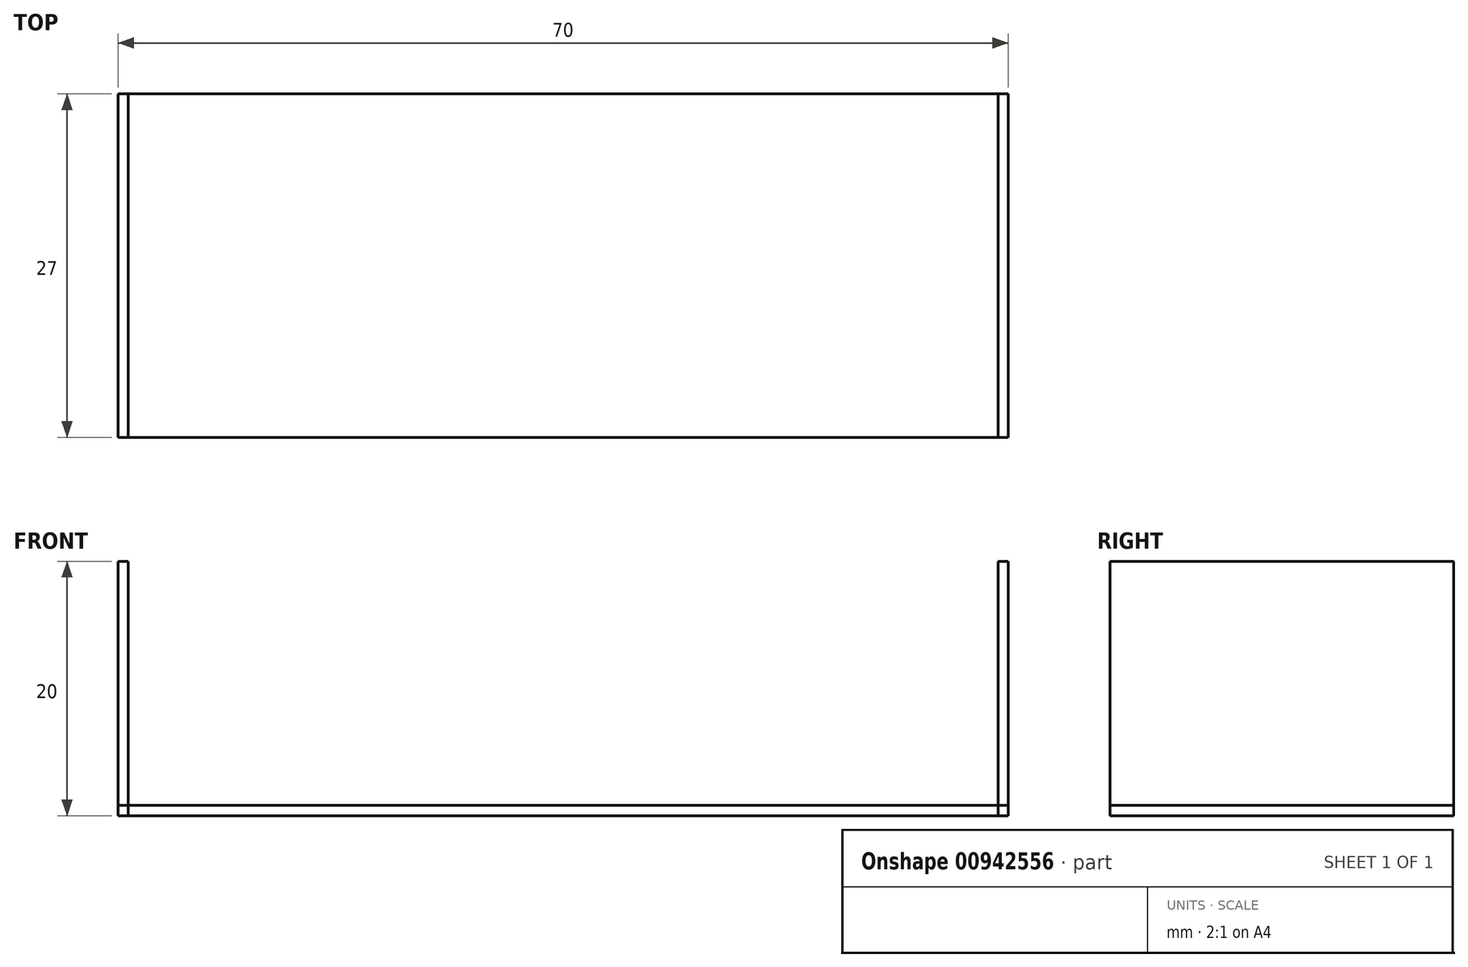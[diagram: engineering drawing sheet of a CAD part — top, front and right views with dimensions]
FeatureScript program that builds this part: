
annotation { "Feature Type Name" : "Feature", "Feature Type Description" : "" }
export const myFeature = defineFeature(function(context is Context, id is Id, definition is map)
    precondition{}
    {
        {
            var Q0;
            Q0=qCreatedBy(makeId("Top.planeOp"),FACE);
            var sketch = newSketch(context, id + "F0", { "sketchPlane" : qUnion([Q0])});
            skLineSegment(sketch, "E0.bottom", {"start": v(35, 13.5) * mm, "end": v(-35, 13.5) * mm});
            skLineSegment(sketch, "E0.top", {"start": v(35, -13.5) * mm, "end": v(-35, -13.5) * mm});
            skLineSegment(sketch, "E0.left", {"start": v(35, 13.5) * mm, "end": v(35, -13.5) * mm});
            skLineSegment(sketch, "E0.right", {"start": v(-35, 13.5) * mm, "end": v(-35, -13.5) * mm});
            skPoint(sketch, "E0.middle", {"position": v(0, 0) * mm});
            skLineSegment(sketch, "E1.bottom", {"start": v(-35, 13.5) * mm, "end": v(-34.2, 13.5) * mm});
            skLineSegment(sketch, "E1.top", {"start": v(-35, -13.5) * mm, "end": v(-34.2, -13.5) * mm});
            skLineSegment(sketch, "E1.right", {"start": v(-34.2, 13.5) * mm, "end": v(-34.2, -13.5) * mm});
            skLineSegment(sketch, "E2.bottom", {"start": v(35, 13.5) * mm, "end": v(34.2, 13.5) * mm});
            skLineSegment(sketch, "E2.top", {"start": v(35, -13.5) * mm, "end": v(34.2, -13.5) * mm});
            skLineSegment(sketch, "E2.right", {"start": v(34.2, 13.5) * mm, "end": v(34.2, -13.5) * mm});
            skSolve(sketch);
        }
        {
            var Q0;
            {var subQ0=sQuery(id+"F0.wireOp",EDGE,"E0.right");Q0=makeQuery(id+"F0.imprint","IMPRINT",FACE,{"disambiguationData":[TD([[makeQuery(id+"F0.imprint","IMPRINT",EDGE,{"derivedFrom":subQ0}),1.0]])]});}
            var Q1;
            {var subQ2=sQuery(id+"F0.wireOp",EDGE,"E0.left");Q1=makeQuery(id+"F0.imprint","IMPRINT",FACE,{"disambiguationData":[TD([[makeQuery(id+"F0.imprint","IMPRINT",EDGE,{"derivedFrom":subQ2}),-1.0]])]});}
            extrude(context, id + "F1", {"entities" : qUnion([Q0, Q1]), "depth" : 20 * mm, "offsetDistance" : 25 * mm});
        }
        {
            var Q0;
            {var subQ3=sQuery(id+"F0.wireOp",EDGE,"E1.right");var subQ8=makeQuery(id+"F0.imprint","IMPRINT",EDGE,{"derivedFrom":subQ3});var subQ10=sQuery(id+"F0.wireOp",EDGE,"E0.left");var subQ11=sQuery(id+"F0.wireOp",EDGE,"E0.right");Q0=qUnion([makeQuery(id+"F0.imprint","IMPRINT",FACE,{"disambiguationData":[TD([[makeQuery(id+"F0.imprint","IMPRINT",EDGE,{"derivedFrom":subQ11}),1.0]])]}),makeQuery(id+"F0.imprint","IMPRINT",FACE,{"disambiguationData":[TD([[makeQuery(id+"F0.imprint","IMPRINT",EDGE,{"derivedFrom":subQ10}),-1.0]])]}),makeQuery(id+"F0.imprint","IMPRINT",FACE,{"disambiguationData":[TD([[subQ8,1.0]])]})]);}
            extrude(context, id + "F2", {"entities" : qUnion([Q0]), "depth" : 0.8 * mm, "offsetDistance" : 25 * mm});
        }
    });
